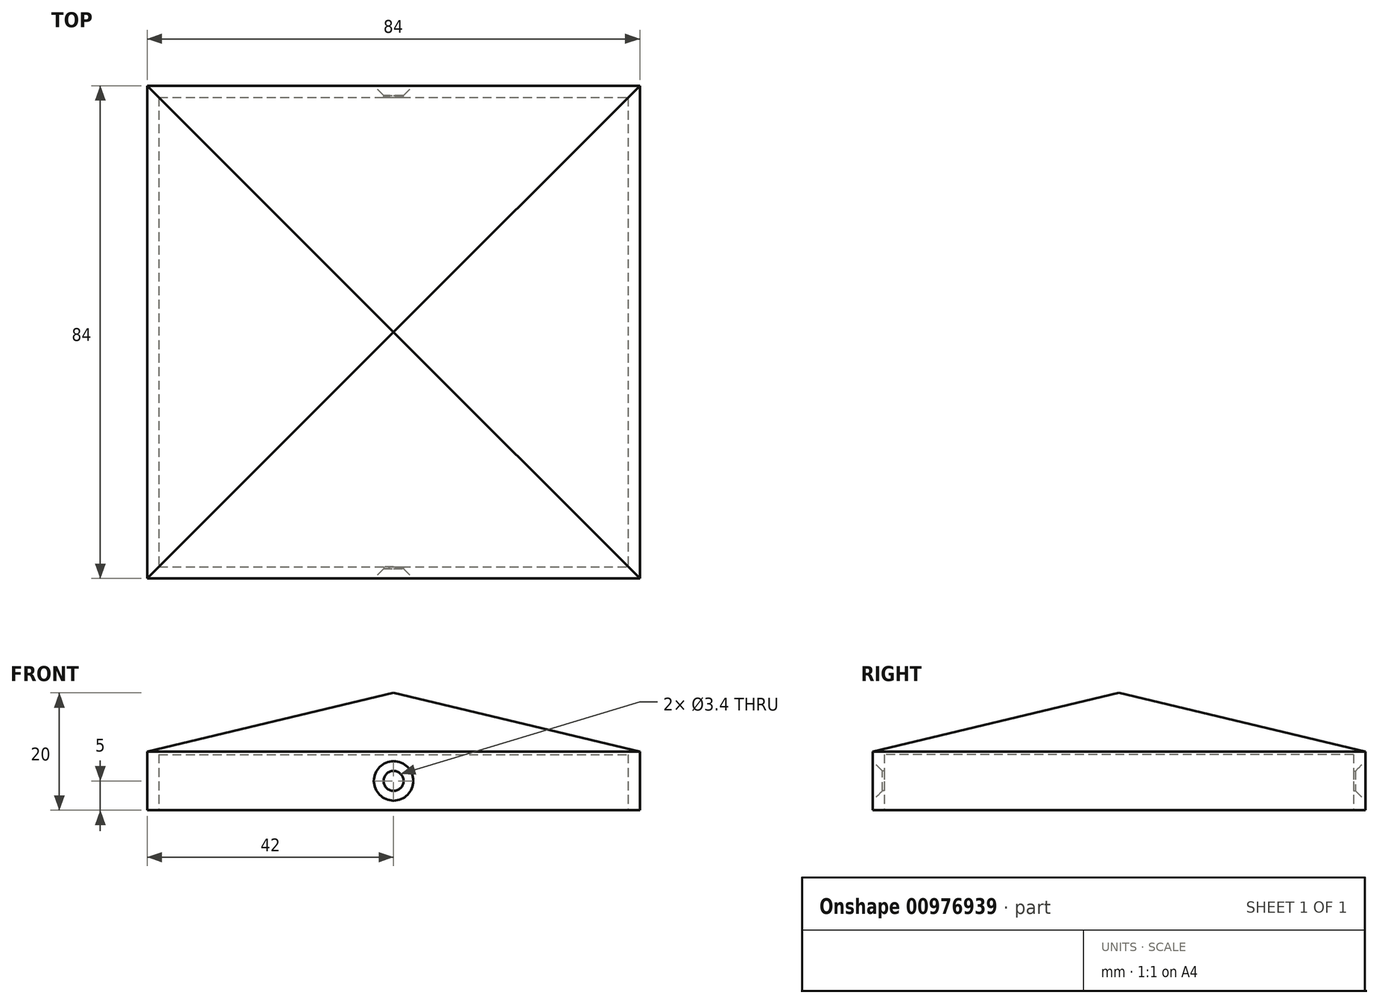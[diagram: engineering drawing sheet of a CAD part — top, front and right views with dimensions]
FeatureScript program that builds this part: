
annotation { "Feature Type Name" : "Feature", "Feature Type Description" : "" }
export const myFeature = defineFeature(function(context is Context, id is Id, definition is map)
    precondition{}
    {
        {
            var Q0;
            Q0=qCreatedBy(makeId("Top.planeOp"),FACE);
            var sketch = newSketch(context, id + "F0", { "sketchPlane" : qUnion([Q0])});
            skLineSegment(sketch, "E0.bottom", {"start": v(0, 0) * mm, "end": v(84, 0) * mm});
            skLineSegment(sketch, "E0.top", {"start": v(0, 84) * mm, "end": v(84, 84) * mm});
            skLineSegment(sketch, "E0.left", {"start": v(0, 0) * mm, "end": v(0, 84) * mm});
            skLineSegment(sketch, "E0.right", {"start": v(84, 0) * mm, "end": v(84, 84) * mm});
            skSolve(sketch);
        }
        {
            var Q0;
            Q0=makeQuery(id+"F0.imprint","IMPRINT",FACE,{"disambiguationData":[TD([[makeQuery(id+"F0.imprint","IMPRINT",EDGE,{"derivedFrom":sQuery(id+"F0.wireOp",EDGE,"E0.bottom")}),1.0]])]});
            extrude(context, id + "F1", {"entities" : qUnion([Q0]), "depth" : 10 * mm, "offsetDistance" : 25 * mm});
        }
        {
            var Q0;
            Q0=makeQuery(id+"F1.opExtrude","CAP_FACE",FACE,{"disambiguationData":[OSD([sQuery(id+"F0.wireOp",EDGE,"E0.bottom"),sQuery(id+"F0.wireOp",EDGE,"E0.top"),sQuery(id+"F0.wireOp",EDGE,"E0.left"),sQuery(id+"F0.wireOp",EDGE,"E0.right")])],"isStart":true});
            var sketch = newSketch(context, id + "F2", { "sketchPlane" : qUnion([Q0])});
            skLineSegment(sketch, "E1.bottom", {"start": v(2, -82) * mm, "end": v(82, -82) * mm});
            skLineSegment(sketch, "E1.top", {"start": v(2, -2) * mm, "end": v(82, -2) * mm});
            skLineSegment(sketch, "E1.left", {"start": v(2, -82) * mm, "end": v(2, -2) * mm});
            skLineSegment(sketch, "E1.right", {"start": v(82, -82) * mm, "end": v(82, -2) * mm});
            skSolve(sketch);
        }
        {
            var Q0;
            Q0=makeQuery(id+"F2.imprint","IMPRINT",FACE,{"disambiguationData":[TD([[makeQuery(id+"F2.imprint","IMPRINT",EDGE,{"derivedFrom":sQuery(id+"F2.wireOp",EDGE,"E1.bottom")}),1.0]])]});
            extrude(context, id + "F3", {"entities" : qUnion([Q0]), "operationType" : NewBodyOperationType.REMOVE, "oppositeDirection" : true, "depth" : 9.5 * mm, "offsetDistance" : 25 * mm});
        }
        {
            var Q0;
            Q0=makeQuery(id+"F1.opExtrude","CAP_FACE",FACE,{"disambiguationData":[OSD([sQuery(id+"F0.wireOp",EDGE,"E0.bottom"),sQuery(id+"F0.wireOp",EDGE,"E0.top"),sQuery(id+"F0.wireOp",EDGE,"E0.left"),sQuery(id+"F0.wireOp",EDGE,"E0.right")])],"isStart":false});
            var sketch = newSketch(context, id + "F4", { "sketchPlane" : qUnion([Q0])});
            skLineSegment(sketch, "E2.bottom", {"start": v(0, 0) * mm, "end": v(84, 0) * mm});
            skLineSegment(sketch, "E2.top", {"start": v(0, 84) * mm, "end": v(84, 84) * mm});
            skLineSegment(sketch, "E2.left", {"start": v(0, 0) * mm, "end": v(0, 84) * mm});
            skLineSegment(sketch, "E2.right", {"start": v(84, 0) * mm, "end": v(84, 84) * mm});
            skSolve(sketch);
        }
        {
            var Q0;
            Q0=makeQuery(id+"F4.imprint","IMPRINT",FACE,{"disambiguationData":[TD([[makeQuery(id+"F4.imprint","IMPRINT",EDGE,{"derivedFrom":sQuery(id+"F4.wireOp",EDGE,"E2.bottom")}),1.0]])]});
            extrude(context, id + "F5", {"entities" : qUnion([Q0]), "operationType" : NewBodyOperationType.ADD, "depth" : 10 * mm, "offsetDistance" : 25 * mm});
        }
        {
            var Q0;
            Q0=makeQuery(id+"F5.opExtrude","CAP_EDGE",EDGE,{"disambiguationData":[OSD([sQuery(id+"F4.wireOp",EDGE,"E2.left")])],"isStart":false});
            var Q1;
            Q1=makeQuery(id+"F5.opExtrude","CAP_EDGE",EDGE,{"disambiguationData":[OSD([sQuery(id+"F4.wireOp",EDGE,"E2.top")])],"isStart":false});
            var Q2;
            Q2=makeQuery(id+"F5.opExtrude","CAP_EDGE",EDGE,{"disambiguationData":[OSD([sQuery(id+"F4.wireOp",EDGE,"E2.right")])],"isStart":false});
            var Q3;
            Q3=makeQuery(id+"F5.opExtrude","CAP_EDGE",EDGE,{"disambiguationData":[OSD([sQuery(id+"F4.wireOp",EDGE,"E2.bottom")])],"isStart":false});
            chamfer(context, id + "F6", {"entities" : qUnion([Q0, Q1, Q2, Q3]), "chamferType" : ChamferType.TWO_OFFSETS, "width1" : 10 * mm, "oppositeDirection" : false, "width2" : 42 * mm, "tangentPropagation" : true});
        }
        {
            var Q0;
            Q0=makeQuery(id+"F5.boolean.opBoolean","MERGE",FACE,{"derivedFrom":[makeQuery(id+"F1.opExtrude","SWEPT_FACE",FACE,{"disambiguationData":[OSD([sQuery(id+"F0.wireOp",EDGE,"E0.bottom")])]}),makeQuery(id+"F5.opExtrude","SWEPT_FACE",FACE,{"disambiguationData":[OSD([sQuery(id+"F4.wireOp",EDGE,"E2.bottom")])]})]});
            var sketch = newSketch(context, id + "F7", { "sketchPlane" : qUnion([Q0])});
            skLineSegment(sketch, "E3.bottom", {"start": v(0, 0) * mm, "end": v(42, 0) * mm});
            skLineSegment(sketch, "E3.top", {"start": v(0, 5) * mm, "end": v(42, 5) * mm});
            skLineSegment(sketch, "E3.left", {"start": v(0, 0) * mm, "end": v(0, 5) * mm});
            skLineSegment(sketch, "E3.right", {"start": v(42, 0) * mm, "end": v(42, 5) * mm});
            skSolve(sketch);
        }
        {
            var Q0;
            Q0=sQuery(id+"F7.wireOp",VERTEX,"E3.top.end");
            var Q1;
            Q1=makeQuery(id+"F1.opExtrude","SWEPT_BODY",BODY,{"disambiguationData":[OSD([sQuery(id+"F0.wireOp",EDGE,"E0.bottom"),sQuery(id+"F0.wireOp",EDGE,"E0.top"),sQuery(id+"F0.wireOp",EDGE,"E0.left"),sQuery(id+"F0.wireOp",EDGE,"E0.right")])]});
            hole(context, id + "F8", {"style" : HoleStyle.C_SINK, "endStyle" : HoleEndStyle.BLIND, "standardTappedOrClearance" : lookupTablePath({ "fit" : "Normal", "standard" : "ISO", "size" : "M3", "type" : "Clearance" }), "standardBlindInLast" : lookupTablePath({ "fit" : "Normal", "standard" : "ISO", "engagement" : "75%", "pitch" : "0.5 mm", "size" : "M3", "type" : "Clearance & tapped" }), "holeDiameter" : 3.4 * mm, "cSinkDiameter" : 6.72 * mm, "cSinkAngle" : 90 * degree, "majorDiameter" : 5 * mm, "holeDepth" : 12 * mm, "isTappedThrough" : true, "tappedDepth" : 12 * mm, "tapClearance" : 3, "locations" : qUnion([Q0]), "scope" : qUnion([Q1])});
        }
        {
            var Q0;
            Q0=makeQuery(id+"F5.boolean.opBoolean","MERGE",FACE,{"derivedFrom":[makeQuery(id+"F1.opExtrude","SWEPT_FACE",FACE,{"disambiguationData":[OSD([sQuery(id+"F0.wireOp",EDGE,"E0.top")])]}),makeQuery(id+"F5.opExtrude","SWEPT_FACE",FACE,{"disambiguationData":[OSD([sQuery(id+"F4.wireOp",EDGE,"E2.top")])]})]});
            var sketch = newSketch(context, id + "F9", { "sketchPlane" : qUnion([Q0])});
            skLineSegment(sketch, "E4.bottom", {"start": v(-84, 0) * mm, "end": v(-42, 0) * mm});
            skLineSegment(sketch, "E4.top", {"start": v(-84, 5) * mm, "end": v(-42, 5) * mm});
            skLineSegment(sketch, "E4.left", {"start": v(-84, 0) * mm, "end": v(-84, 5) * mm});
            skLineSegment(sketch, "E4.right", {"start": v(-42, 0) * mm, "end": v(-42, 5) * mm});
            skSolve(sketch);
        }
        {
            var Q0;
            Q0=sQuery(id+"F9.wireOp",VERTEX,"E4.top.end");
            var Q1;
            Q1=makeQuery(id+"F1.opExtrude","SWEPT_BODY",BODY,{"disambiguationData":[OSD([sQuery(id+"F0.wireOp",EDGE,"E0.bottom"),sQuery(id+"F0.wireOp",EDGE,"E0.top"),sQuery(id+"F0.wireOp",EDGE,"E0.left"),sQuery(id+"F0.wireOp",EDGE,"E0.right")])]});
            hole(context, id + "F10", {"style" : HoleStyle.C_SINK, "endStyle" : HoleEndStyle.BLIND, "standardTappedOrClearance" : lookupTablePath({ "fit" : "Normal", "standard" : "ISO", "size" : "M3", "type" : "Clearance" }), "standardBlindInLast" : lookupTablePath({ "fit" : "Normal", "standard" : "ISO", "engagement" : "75%", "pitch" : "0.5 mm", "size" : "M3", "type" : "Clearance & tapped" }), "holeDiameter" : 3.4 * mm, "cSinkDiameter" : 6.72 * mm, "cSinkAngle" : 90 * degree, "majorDiameter" : 5 * mm, "holeDepth" : 12 * mm, "isTappedThrough" : true, "tappedDepth" : 12 * mm, "tapClearance" : 3, "locations" : qUnion([Q0]), "scope" : qUnion([Q1])});
        }
    });
